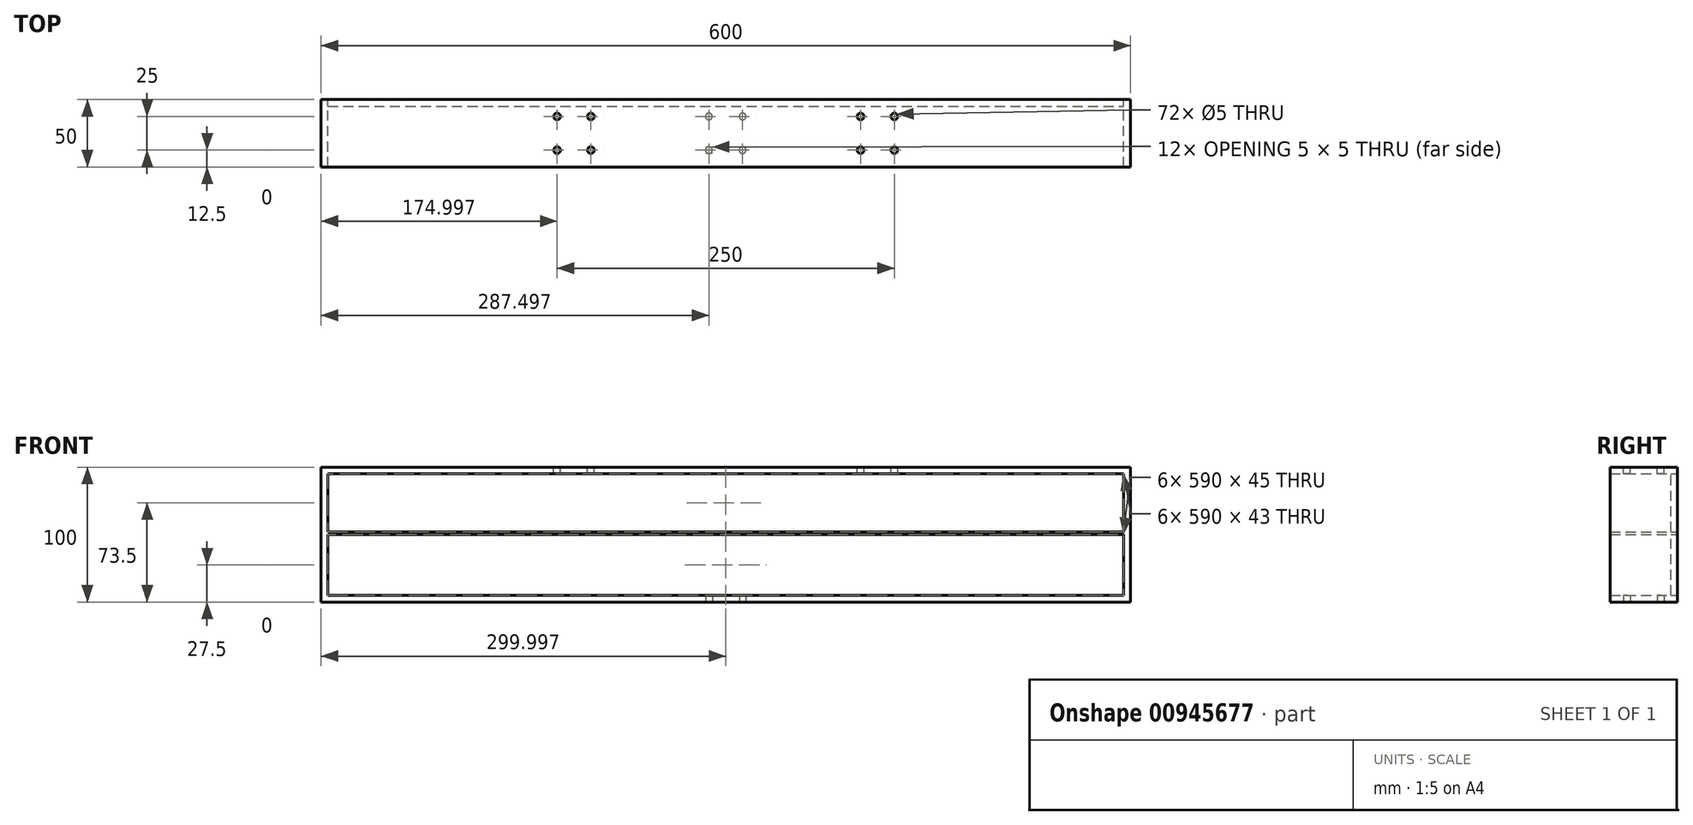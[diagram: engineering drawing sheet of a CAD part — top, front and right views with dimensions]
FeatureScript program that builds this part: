
annotation { "Feature Type Name" : "Feature", "Feature Type Description" : "" }
export const myFeature = defineFeature(function(context is Context, id is Id, definition is map)
    precondition{}
    {
        {
            var Q0;
            Q0=qCreatedBy(makeId("Front.planeOp"),FACE);
            var sketch = newSketch(context, id + "F0", { "sketchPlane" : qUnion([Q0])});
            skLineSegment(sketch, "E0.bottom", {"start": v(-200.46, 0) * mm, "end": v(399.54, 0) * mm});
            skLineSegment(sketch, "E0.top", {"start": v(-200.46, 100) * mm, "end": v(399.54, 100) * mm});
            skLineSegment(sketch, "E0.left", {"start": v(-200.46, 0) * mm, "end": v(-200.46, 100) * mm});
            skLineSegment(sketch, "E0.right", {"start": v(399.54, 0) * mm, "end": v(399.54, 100) * mm});
            skLineSegment(sketch, "E1", {"start": v(-195.46, 0) * mm, "end": v(-195.46, 100) * mm});
            skLineSegment(sketch, "E2", {"start": v(394.54, 0) * mm, "end": v(394.54, 100) * mm});
            skPoint(sketch, "E2.endSnap0", {"position": v(99.54, 100) * mm});
            skLineSegment(sketch, "E3", {"start": v(-195.46, 95) * mm, "end": v(394.54, 95) * mm});
            skLineSegment(sketch, "E4", {"start": v(-195.46, 5) * mm, "end": v(394.54, 5) * mm});
            skLineSegment(sketch, "E5", {"start": v(-195.46, 52) * mm, "end": v(394.54, 52) * mm});
            skLineSegment(sketch, "E6", {"start": v(394.54, 50) * mm, "end": v(-195.46, 50) * mm});
            skSolve(sketch);
        }
        {
            var Q0;
            {var subQ0=sQuery(id+"F0.wireOp",EDGE,"E4");Q0=makeQuery(id+"F0.imprint","IMPRINT",FACE,{"disambiguationData":[TD([[makeQuery(id+"F0.imprint","IMPRINT",EDGE,{"derivedFrom":subQ0}),1.0]])]});}
            var Q1;
            {var subQ0=sQuery(id+"F0.wireOp",EDGE,"E3");Q1=makeQuery(id+"F0.imprint","IMPRINT",FACE,{"disambiguationData":[TD([[makeQuery(id+"F0.imprint","IMPRINT",EDGE,{"derivedFrom":subQ0}),-1.0]])]});}
            extrude(context, id + "F1", {"entities" : qUnion([Q0, Q1]), "depth" : 5 * mm, "offsetDistance" : 25 * mm});
        }
        {
            var Q0;
            {var subQ0=sQuery(id+"F0.wireOp",EDGE,"E0.left");Q0=makeQuery(id+"F0.imprint","IMPRINT",FACE,{"disambiguationData":[TD([[makeQuery(id+"F0.imprint","IMPRINT",EDGE,{"derivedFrom":subQ0}),-1.0]])]});}
            var Q1;
            {var subQ5=sQuery(id+"F0.wireOp",EDGE,"E4");Q1=makeQuery(id+"F0.imprint","IMPRINT",FACE,{"disambiguationData":[TD([[makeQuery(id+"F0.imprint","IMPRINT",EDGE,{"derivedFrom":subQ5}),-1.0]])]});}
            var Q2;
            {var subQ0=sQuery(id+"F0.wireOp",EDGE,"E5");Q2=makeQuery(id+"F0.imprint","IMPRINT",FACE,{"disambiguationData":[TD([[makeQuery(id+"F0.imprint","IMPRINT",EDGE,{"derivedFrom":subQ0}),-1.0]])]});}
            var Q3;
            {var subQ5=sQuery(id+"F0.wireOp",EDGE,"E3");Q3=makeQuery(id+"F0.imprint","IMPRINT",FACE,{"disambiguationData":[TD([[makeQuery(id+"F0.imprint","IMPRINT",EDGE,{"derivedFrom":subQ5}),1.0]])]});}
            var Q4;
            {var subQ4=sQuery(id+"F0.wireOp",EDGE,"E0.right");Q4=makeQuery(id+"F0.imprint","IMPRINT",FACE,{"disambiguationData":[TD([[makeQuery(id+"F0.imprint","IMPRINT",EDGE,{"derivedFrom":subQ4}),1.0]])]});}
            extrude(context, id + "F2", {"entities" : qUnion([Q0, Q1, Q2, Q3, Q4]), "depth" : 50 * mm, "offsetDistance" : 25 * mm});
        }
        {
            var Q0;
            Q0=qCreatedBy(makeId("Top.planeOp"),FACE);
            var sketch = newSketch(context, id + "F3", { "sketchPlane" : qUnion([Q0])});
            skPoint(sketch, "E7", {"position": v(87.04, -37.5) * mm});
            skPoint(sketch, "E8", {"position": v(112.04, -37.5) * mm});
            skPoint(sketch, "E9", {"position": v(87.04, -12.5) * mm});
            skPoint(sketch, "E10", {"position": v(112.04, -12.5) * mm});
            skSolve(sketch);
        }
        {
            var Q0;
            Q0=sQuery(id+"F3.wireOp",VERTEX,"E7");
            var Q1;
            Q1=sQuery(id+"F3.wireOp",VERTEX,"E8");
            var Q2;
            Q2=sQuery(id+"F3.wireOp",VERTEX,"E10");
            var Q3;
            Q3=sQuery(id+"F3.wireOp",VERTEX,"E9");
            var Q4;
            Q4=makeQuery(id+"F2.opExtrude","SWEPT_BODY",BODY,{"disambiguationData":[OSD([sQuery(id+"F0.wireOp",EDGE,"E0.bottom"),sQuery(id+"F0.wireOp",EDGE,"E0.top"),sQuery(id+"F0.wireOp",EDGE,"E0.left"),sQuery(id+"F0.wireOp",EDGE,"E0.right"),sQuery(id+"F0.wireOp",EDGE,"E1"),sQuery(id+"F0.wireOp",EDGE,"E2"),sQuery(id+"F0.wireOp",EDGE,"E3"),sQuery(id+"F0.wireOp",EDGE,"E4"),sQuery(id+"F0.wireOp",EDGE,"E5"),sQuery(id+"F0.wireOp",EDGE,"E6")])]});
            hole(context, id + "F4", {"style" : HoleStyle.SIMPLE, "endStyle" : HoleEndStyle.BLIND, "oppositeDirection" : true, "standardTappedOrClearance" : lookupTablePath({ "standard" : "ISO", "size" : "5", "type" : "Drilled" }), "standardBlindInLast" : lookupTablePath({ "standard" : "ISO", "size" : "5", "type" : "Drilled" }), "holeDiameter" : 5 * mm, "majorDiameter" : 5 * mm, "holeDepth" : 12 * mm, "isTappedThrough" : true, "tappedDepth" : 12 * mm, "tapClearance" : 3, "locations" : qUnion([Q0, Q1, Q2, Q3]), "scope" : qUnion([Q4])});
        }
        {
            var Q0;
            Q0=makeQuery(id+"F2.opExtrude","SWEPT_FACE",FACE,{"disambiguationData":[OSD([sQuery(id+"F0.wireOp",EDGE,"E0.top")])]});
            var sketch = newSketch(context, id + "F5", { "sketchPlane" : qUnion([Q0])});
            skPoint(sketch, "E11", {"position": v(-25.46, -12.5) * mm});
            skPoint(sketch, "E12", {"position": v(-0.46, -12.5) * mm});
            skPoint(sketch, "E13", {"position": v(-0.46, -37.5) * mm});
            skPoint(sketch, "E14", {"position": v(-25.46, -37.5) * mm});
            skPoint(sketch, "E15", {"position": v(199.54, -12.5) * mm});
            skPoint(sketch, "E16", {"position": v(224.54, -12.5) * mm});
            skPoint(sketch, "E17", {"position": v(199.54, -37.5) * mm});
            skPoint(sketch, "E18", {"position": v(224.54, -37.5) * mm});
            skSolve(sketch);
        }
        {
            var Q0;
            Q0=sQuery(id+"F5.wireOp",VERTEX,"E15");
            var Q1;
            Q1=sQuery(id+"F5.wireOp",VERTEX,"E16");
            var Q2;
            Q2=sQuery(id+"F5.wireOp",VERTEX,"E18");
            var Q3;
            Q3=sQuery(id+"F5.wireOp",VERTEX,"E17");
            var Q4;
            Q4=sQuery(id+"F5.wireOp",VERTEX,"E11");
            var Q5;
            Q5=sQuery(id+"F5.wireOp",VERTEX,"E12");
            var Q6;
            Q6=sQuery(id+"F5.wireOp",VERTEX,"E13");
            var Q7;
            Q7=sQuery(id+"F5.wireOp",VERTEX,"E14");
            var Q8;
            Q8=makeQuery(id+"F2.opExtrude","SWEPT_BODY",BODY,{"disambiguationData":[OSD([sQuery(id+"F0.wireOp",EDGE,"E0.bottom"),sQuery(id+"F0.wireOp",EDGE,"E0.top"),sQuery(id+"F0.wireOp",EDGE,"E0.left"),sQuery(id+"F0.wireOp",EDGE,"E0.right"),sQuery(id+"F0.wireOp",EDGE,"E1"),sQuery(id+"F0.wireOp",EDGE,"E2"),sQuery(id+"F0.wireOp",EDGE,"E3"),sQuery(id+"F0.wireOp",EDGE,"E4"),sQuery(id+"F0.wireOp",EDGE,"E5"),sQuery(id+"F0.wireOp",EDGE,"E6")])]});
            hole(context, id + "F6", {"style" : HoleStyle.SIMPLE, "endStyle" : HoleEndStyle.BLIND, "standardTappedOrClearance" : lookupTablePath({ "standard" : "ISO", "size" : "5", "type" : "Drilled" }), "standardBlindInLast" : lookupTablePath({ "standard" : "ISO", "size" : "5", "type" : "Drilled" }), "holeDiameter" : 5 * mm, "majorDiameter" : 5 * mm, "holeDepth" : 12 * mm, "isTappedThrough" : true, "tappedDepth" : 12 * mm, "tapClearance" : 3, "locations" : qUnion([Q0, Q1, Q2, Q3, Q4, Q5, Q6, Q7]), "scope" : qUnion([Q8])});
        }
    });
